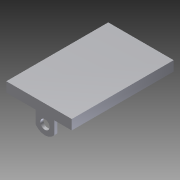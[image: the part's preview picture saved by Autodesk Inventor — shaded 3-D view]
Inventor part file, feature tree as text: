
AUTODESK INVENTOR PART (.ipt)
format: ipt  version: 2011 SP1 (Build 150282100, 282)  size: 104,448 bytes
history: native  units: in
note: dims shown in document units (in); Inventor stores cm internally (conversion verified against a paired STEP export)
features: other x42, extrude x3, sketch x3
ambient origin geometry x8: Origin, YZ Plane, XZ Plane, XY Plane, X Axis, Y Axis, Z Axis, Center Point
bodies: Solid1 (feature_tree), body_to_terminal_XY (feature_tree), body_to_terminal_YZ (feature_tree), body_to_terminal_ZX (feature_tree), body_to_terminal_X (feature_tree), body_to_terminal_Y (feature_tree), body_to_terminal_Z (feature_tree), body_to_terminal_Center (feature_tree)
feature tree (48):
  extrude  "Extrusion1"  Depth=0.031in TaperAngle=0.0deg
  extrude  "Extrusion2"  [1 undecoded]
  extrude  "Extrusion3"  [1 undecoded]
  other  "wire_1_XY"
  other  "wire_1_YZ"
  other  "wire_1_ZX"
  other  "wire_1_X"
  other  "wire_1_Y"
  other  "wire_1_Z"
  other  "wire_1_Center"
  other  "wire_2_XY"
  other  "wire_2_YZ"
  other  "wire_2_ZX"
  other  "wire_2_X"
  other  "wire_2_Y"
  other  "wire_2_Z"
  other  "wire_2_Center"
  other  "wire_3_XY"
  other  "wire_3_YZ"
  other  "wire_3_ZX"
  other  "wire_3_X"
  other  "wire_3_Y"
  other  "wire_3_Z"
  other  "wire_3_Center"
  other  "wire_4_XY"
  other  "wire_4_YZ"
  other  "wire_4_ZX"
  other  "wire_4_X"
  other  "wire_4_Y"
  other  "wire_4_Z"
  other  "wire_4_Center"
  other  "wire_5_XY"
  other  "wire_5_YZ"
  other  "wire_5_ZX"
  other  "wire_5_X"
  other  "wire_5_Y"
  other  "wire_5_Z"
  other  "wire_5_Center"
  other  "wire_6_XY"
  other  "wire_6_YZ"
  other  "wire_6_ZX"
  other  "wire_6_X"
  other  "wire_6_Y"
  other  "wire_6_Z"
  other  "wire_6_Center"
  sketch  "Sketch_2"  dims[d4=0.031in d5=0.0in]
  sketch  "Sketch_1"  dims[d0=0.1in d1=0.0in d2=0.031in d3=0.0in]
  sketch  "Sketch_3"
note: 2 required parameter values undecoded (feature->parameter linkage not recoverable at this tier; creation-order binding heuristic only, values carry confidence <= 0.55)
